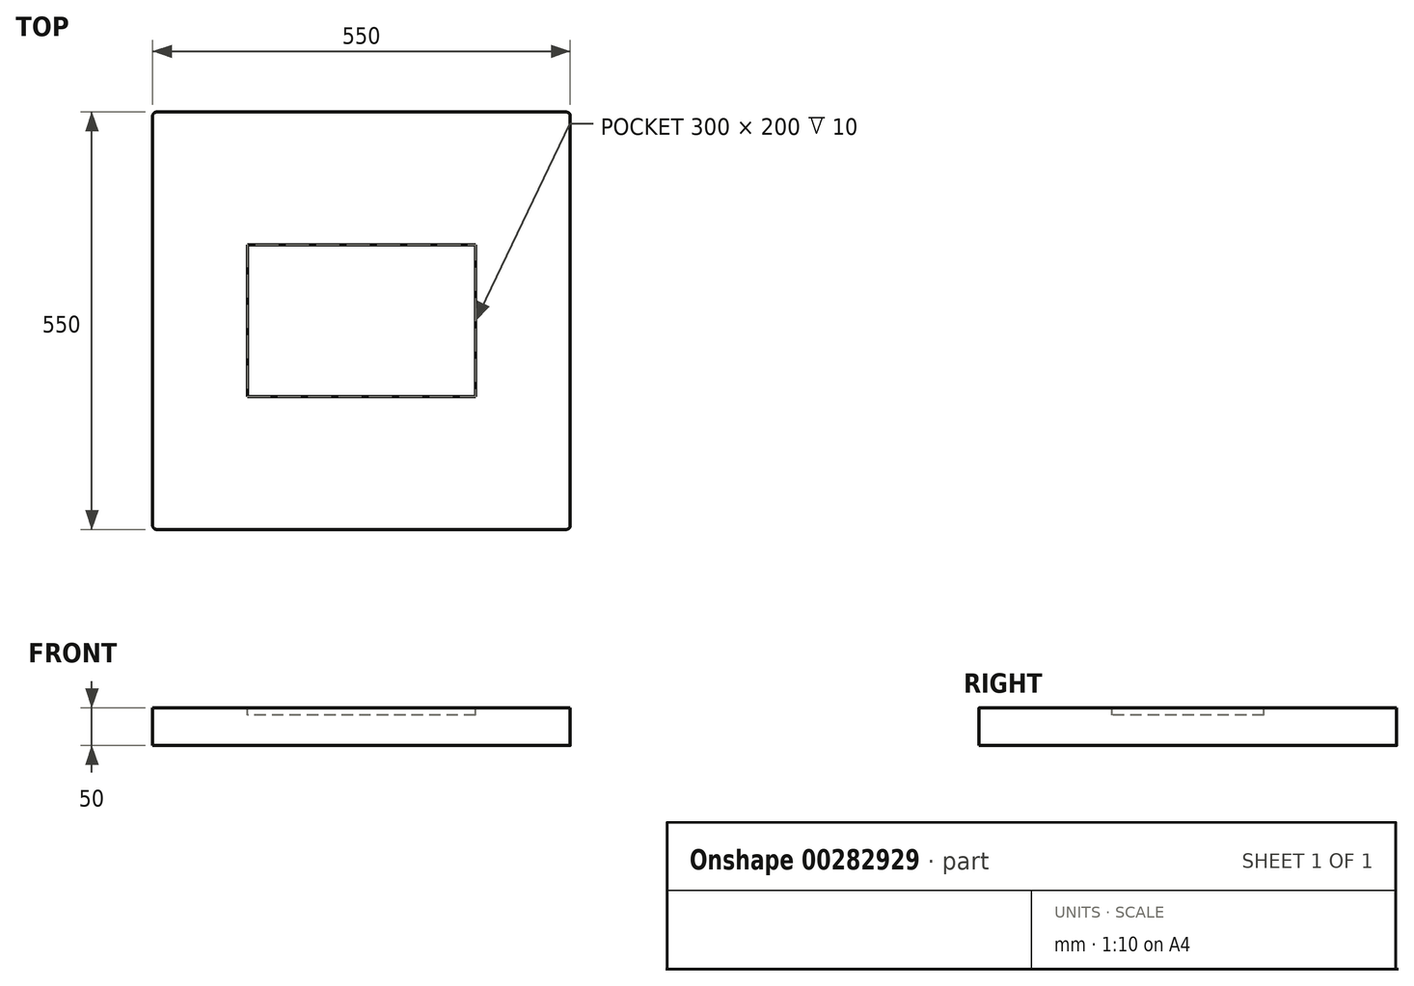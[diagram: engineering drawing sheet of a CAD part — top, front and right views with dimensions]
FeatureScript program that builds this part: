
annotation { "Feature Type Name" : "Feature", "Feature Type Description" : "" }
export const myFeature = defineFeature(function(context is Context, id is Id, definition is map)
    precondition{}
    {
        {
            var Q0;
            Q0=qCreatedBy(makeId("Top.planeOp"),FACE);
            var sketch = newSketch(context, id + "F0", { "sketchPlane" : qUnion([Q0])});
            skLineSegment(sketch, "E0.bottom", {"start": v(275, 275) * mm, "end": v(-275, 275) * mm});
            skLineSegment(sketch, "E0.top", {"start": v(275, -275) * mm, "end": v(-275, -275) * mm});
            skLineSegment(sketch, "E0.left", {"start": v(275, 275) * mm, "end": v(275, -275) * mm});
            skLineSegment(sketch, "E0.right", {"start": v(-275, 275) * mm, "end": v(-275, -275) * mm});
            skPoint(sketch, "E0.middle", {"position": v(0, 0) * mm});
            skSolve(sketch);
        }
        {
            var Q0;
            Q0=makeQuery(id+"F0.imprint","IMPRINT",FACE,{"disambiguationData":[TD([[makeQuery(id+"F0.imprint","IMPRINT",EDGE,{"derivedFrom":sQuery(id+"F0.wireOp",EDGE,"E0.bottom")}),1.0]])]});
            extrude(context, id + "F1", {"entities" : qUnion([Q0]), "depth" : 50 * mm});
        }
        {
            var Q0;
            Q0=makeQuery(id+"F1.opExtrude","SWEPT_EDGE",EDGE,{"disambiguationData":[OSD([sQuery(id+"F0.wireOp",EDGE,"E0.top"),sQuery(id+"F0.wireOp",EDGE,"E0.right")])]});
            var Q1;
            Q1=makeQuery(id+"F1.opExtrude","SWEPT_EDGE",EDGE,{"disambiguationData":[OSD([sQuery(id+"F0.wireOp",EDGE,"E0.top"),sQuery(id+"F0.wireOp",EDGE,"E0.left")])]});
            var Q2;
            Q2=makeQuery(id+"F1.opExtrude","SWEPT_EDGE",EDGE,{"disambiguationData":[OSD([sQuery(id+"F0.wireOp",EDGE,"E0.bottom"),sQuery(id+"F0.wireOp",EDGE,"E0.left")])]});
            var Q3;
            Q3=makeQuery(id+"F1.opExtrude","SWEPT_EDGE",EDGE,{"disambiguationData":[OSD([sQuery(id+"F0.wireOp",EDGE,"E0.bottom"),sQuery(id+"F0.wireOp",EDGE,"E0.right")])]});
            fillet(context, id + "F2", {"entities" : qUnion([Q0, Q1, Q2, Q3]), "radius" : 5 * mm, "tangentPropagation" : true, "allowEdgeOverflow" : false});
        }
        {
            var Q0;
            Q0=makeQuery(id+"F1.opExtrude","CAP_FACE",FACE,{"disambiguationData":[OSD([sQuery(id+"F0.wireOp",EDGE,"E0.bottom"),sQuery(id+"F0.wireOp",EDGE,"E0.top"),sQuery(id+"F0.wireOp",EDGE,"E0.left"),sQuery(id+"F0.wireOp",EDGE,"E0.right")])],"isStart":false});
            var sketch = newSketch(context, id + "F3", { "sketchPlane" : qUnion([Q0])});
            skLineSegment(sketch, "E1.bottom", {"start": v(150, 100) * mm, "end": v(-150, 100) * mm});
            skLineSegment(sketch, "E1.top", {"start": v(150, -100) * mm, "end": v(-150, -100) * mm});
            skLineSegment(sketch, "E1.left", {"start": v(150, 100) * mm, "end": v(150, -100) * mm});
            skLineSegment(sketch, "E1.right", {"start": v(-150, 100) * mm, "end": v(-150, -100) * mm});
            skPoint(sketch, "E1.middle", {"position": v(0, 0) * mm});
            skSolve(sketch);
        }
        {
            var Q0;
            Q0=makeQuery(id+"F3.imprint","IMPRINT",FACE,{"disambiguationData":[TD([[makeQuery(id+"F3.imprint","IMPRINT",EDGE,{"derivedFrom":sQuery(id+"F3.wireOp",EDGE,"E1.bottom")}),1.0]])]});
            extrude(context, id + "F4", {"entities" : qUnion([Q0]), "operationType" : NewBodyOperationType.REMOVE, "oppositeDirection" : true, "depth" : 10 * mm});
        }
    });
